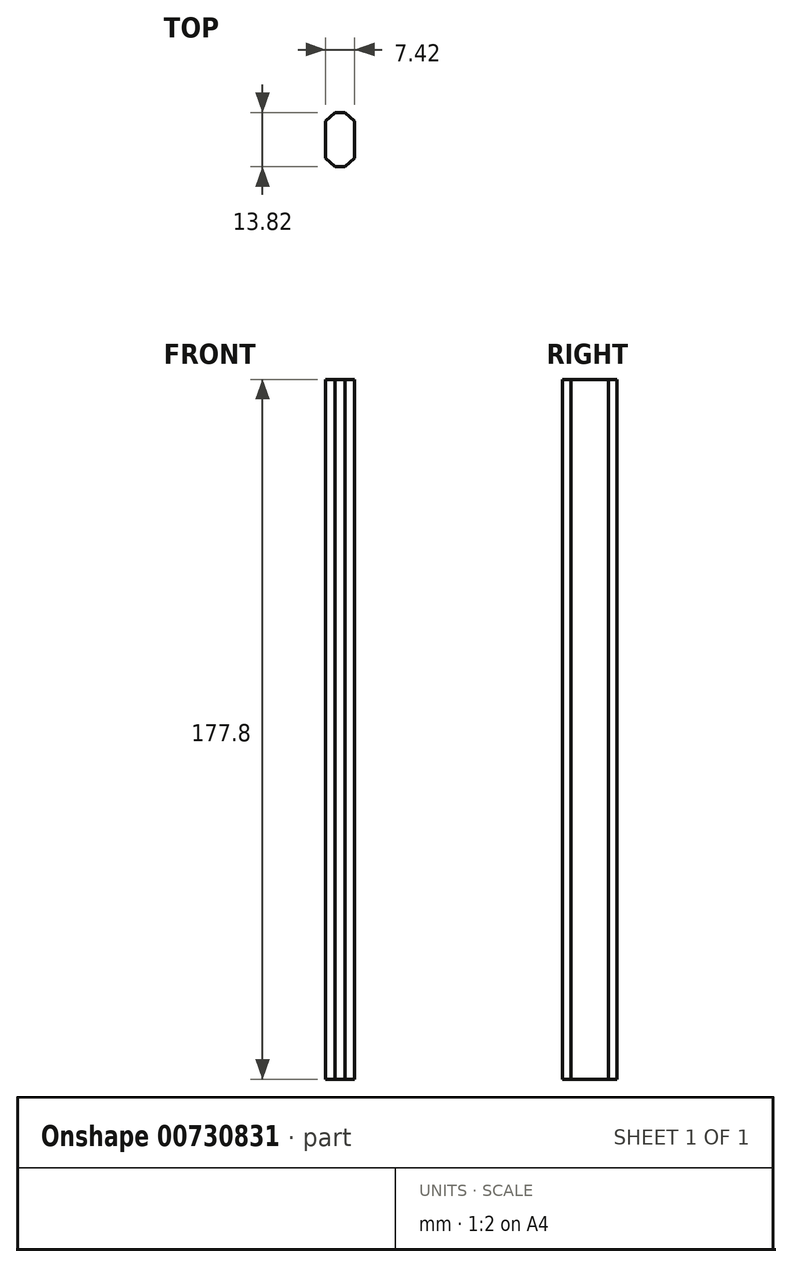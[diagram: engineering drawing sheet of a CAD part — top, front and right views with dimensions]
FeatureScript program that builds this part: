
annotation { "Feature Type Name" : "Feature", "Feature Type Description" : "" }
export const myFeature = defineFeature(function(context is Context, id is Id, definition is map)
    precondition{}
    {
        {
            var Q0;
            Q0=qCreatedBy(makeId("Top.planeOp"),FACE);
            var sketch = newSketch(context, id + "F0", { "sketchPlane" : qUnion([Q0])});
            skLineSegment(sketch, "E0.MirrorCS", {"start": v(3.72, 9.5) * mm, "end": v(3.71, 4.75) * mm});
            skLineSegment(sketch, "E1.MirrorCS", {"start": v(0, 11.66) * mm, "end": v(1.3, 11.66) * mm});
            skLineSegment(sketch, "E2.MirrorCS", {"start": v(1.3, 11.66) * mm, "end": v(3.72, 9.5) * mm});
            skPoint(sketch, "E3.MirrorCS.end.orphan", {"position": v(3.71, 0) * mm});
            skPoint(sketch, "E3.MirrorCS.start.orphan", {"position": v(3.71, -11.92) * mm});
            skPoint(sketch, "E4.MirrorCS.start.orphan", {"position": v(2, -14.08) * mm});
            skPoint(sketch, "E5.orphan", {"position": v(-3.71, 0) * mm});
            skLineSegment(sketch, "E6.MirrorCS", {"start": v(3.71, 0) * mm, "end": v(3.71, 4.75) * mm});
            skLineSegment(sketch, "E7.MirrorCS", {"start": v(1.3, -2.16) * mm, "end": v(3.72, 0) * mm});
            skLineSegment(sketch, "E8.MirrorCS", {"start": v(0, -2.16) * mm, "end": v(1.3, -2.16) * mm});
            skLineSegment(sketch, "E9", {"start": v(0, -2.16) * mm, "end": v(0, 11.66) * mm});
            skPoint(sketch, "E10.end.orphan", {"position": v(-3.72, 4.75) * mm});
            skPoint(sketch, "E11.end.orphan", {"position": v(-3.72, 9.5) * mm});
            skLineSegment(sketch, "E12.MirrorCS", {"start": v(-1.3, 11.66) * mm, "end": v(-3.72, 9.5) * mm});
            skLineSegment(sketch, "E13.MirrorCS", {"start": v(-3.72, 9.5) * mm, "end": v(-3.71, 4.75) * mm});
            skLineSegment(sketch, "E14.MirrorCS", {"start": v(-3.71, 0) * mm, "end": v(-3.71, 4.75) * mm});
            skLineSegment(sketch, "E15.MirrorCS", {"start": v(-1.3, -2.16) * mm, "end": v(-3.72, 0) * mm});
            skLineSegment(sketch, "E16.MirrorCS", {"start": v(0, -2.16) * mm, "end": v(-1.3, -2.16) * mm});
            skLineSegment(sketch, "E17.MirrorCS", {"start": v(0, 11.66) * mm, "end": v(-1.3, 11.66) * mm});
            skSolve(sketch);
        }
        {
            var Q0;
            Q0=makeQuery(id+"F0.imprint","IMPRINT",FACE,{"disambiguationData":[TD([[makeQuery(id+"F0.imprint","IMPRINT",EDGE,{"derivedFrom":sQuery(id+"F0.wireOp",EDGE,"E9")}),1.0]])]});
            var Q1;
            Q1=makeQuery(id+"F0.imprint","IMPRINT",FACE,{"disambiguationData":[TD([[makeQuery(id+"F0.imprint","IMPRINT",EDGE,{"derivedFrom":sQuery(id+"F0.wireOp",EDGE,"E0.MirrorCS")}),-1.0]])]});
            extrude(context, id + "F1", {"entities" : qUnion([Q0, Q1]), "depth" : 177.8 * mm, "offsetDistance" : 25 * mm});
        }
    });
